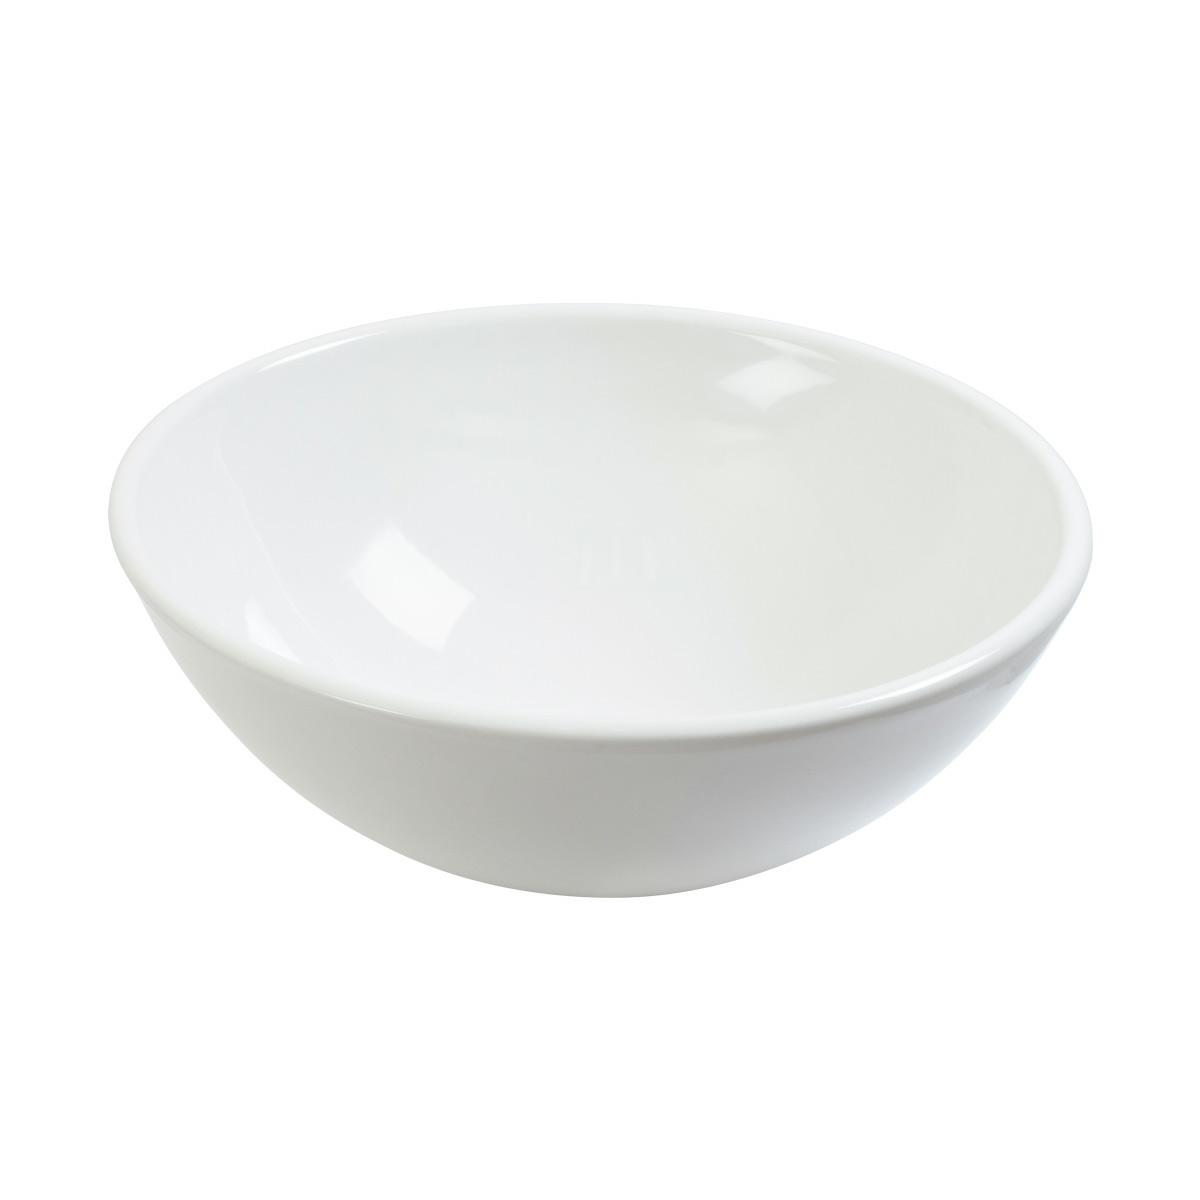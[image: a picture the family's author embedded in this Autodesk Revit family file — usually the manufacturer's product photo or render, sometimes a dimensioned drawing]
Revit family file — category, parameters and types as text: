
# Revit family: CCMX-CORONA_SPAZIO
name_source: partatom
category: Plumbing Fixtures
units: mm (PartAtom-declared; Revit-internal decimal feet)

## family parameters
Always vertical = Yes
Cut with Voids When Loaded = No
OmniClass Number = 23.45.00.00
OmniClass Title = Sanitary, Laundry, and Cleaning Equipment
Part Type = Normal
Room Calculation Point = No
Round Connector Dimension = Use Diameter
Shared = No
Work Plane-Based = No

## types (1)
- CCMX-CORONA_SPAZIO
    Assembly Code = D2010.60
    Description = Lavamanos tipo vessel en porcelana sanitaria. Ideal para espacios minimalistas, simplicidad e innovación en el diseño para baños modernos.
    Dimensiones = https://coronamexico.com
    Ficha Tecnica = https://coronamexico.com
    Garantia de Producto = 20 años en porcelana sanitaria
    Keynote = 224116
    Manufacturer = CORONA
    Model = Spazio
    Type Image = SPAZIO.jpg
    URL = https://coronamexico.com

## geometry (parser evidence)
native form markers: Sweep x3
no freeform markers — native parametric forms only
